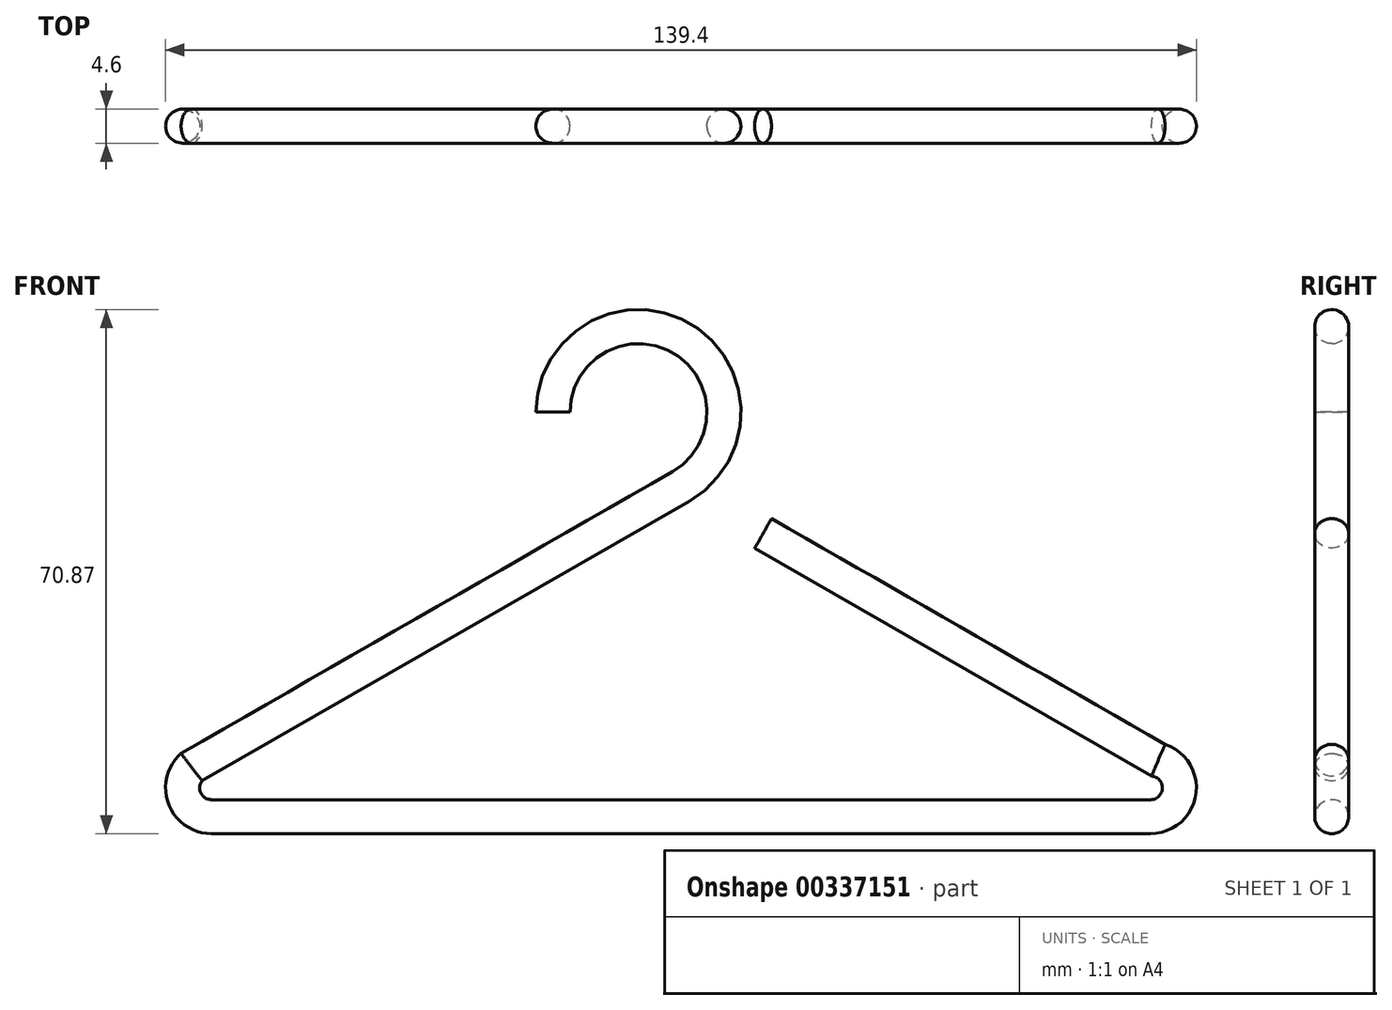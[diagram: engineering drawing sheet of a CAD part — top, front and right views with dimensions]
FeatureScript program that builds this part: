
annotation { "Feature Type Name" : "Feature", "Feature Type Description" : "" }
export const myFeature = defineFeature(function(context is Context, id is Id, definition is map)
    precondition{}
    {
        {
            var Q0;
            Q0=qCreatedBy(makeId("Front.planeOp"),FACE);
            var sketch = newSketch(context, id + "F0", { "sketchPlane" : qUnion([Q0])});
            skLineSegment(sketch, "E0", {"start": v(0, 0) * mm, "end": v(-63.5, 0) * mm});
            skLineSegment(sketch, "E1", {"start": v(0, 0) * mm, "end": v(63.5, 0) * mm});
            skArc(sketch, "E2", {"start": v(-66.22, 6.7) * mm, "mid": v(-67.11, 2.44) * mm, "end": v(-63.5, 0) * mm});
            skArc(sketch, "E3", {"start": v(63.5, 0) * mm, "mid": v(67.36, 3.37) * mm, "end": v(64.55, 7.66) * mm});
            skLineSegment(sketch, "E4", {"start": v(-66.22, 6.7) * mm, "end": v(0, 44.67) * mm});
            skArc(sketch, "E5", {"start": v(0, 44.67) * mm, "mid": v(0.04, 64.7) * mm, "end": v(-17.32, 54.7) * mm});
            skLineSegment(sketch, "E6", {"start": v(64.55, 7.66) * mm, "end": v(11.1, 38.3) * mm});
            skLineSegment(sketch, "E7", {"start": v(-17.32, 54.7) * mm, "end": v(-17.32, 84.5) * mm, "construction": true});
            skSolve(sketch);
        }
        {
            var Q0;
            Q0=qCreatedBy(makeId("Top.planeOp"),FACE);
            var Q1;
            Q1=sQuery(id+"F0.wireOp",VERTEX,"E7.start");
            cPlane(context, id + "F1", {"entities" : qUnion([Q0, Q1]), "cplaneType" : CPlaneType.PLANE_POINT, "offset" : 25.4 * mm, "width" : 152.4 * mm, "height" : 152.4 * mm});
        }
        {
            var Q0;
            Q0=qCreatedBy(id+"F1.planeOp",FACE);
            var sketch = newSketch(context, id + "F2", { "sketchPlane" : qUnion([Q0])});
            skCircle(sketch, "E8", {"center": v(-17.32, 0) * mm, "radius": 2.3 * mm});
            skSolve(sketch);
        }
        {
            var Q0;
            Q0 = qSketchRegion(id + "F2", true);
            var Q1;
            Q1 = qConstructionFilter(qBodyType(qCreatedBy(id + "F0" ,EDGE), BodyType.WIRE), ConstructionObject.NO);
            sweep(context, id + "F3", {"profiles" : qUnion([Q0]), "path" : qUnion([Q1])});
        }
    });
